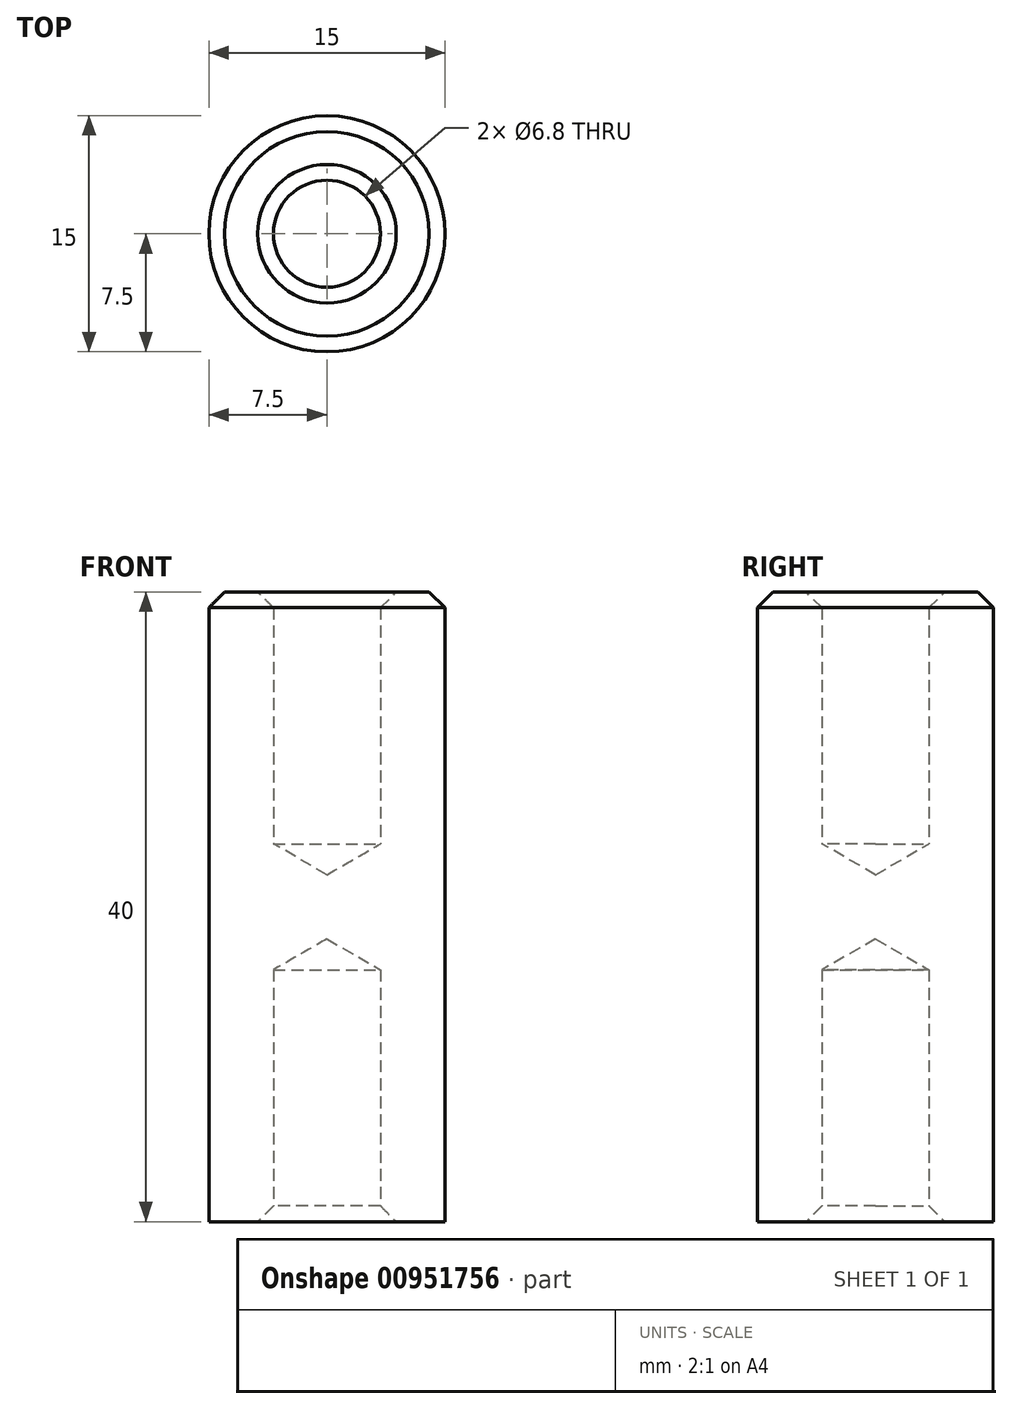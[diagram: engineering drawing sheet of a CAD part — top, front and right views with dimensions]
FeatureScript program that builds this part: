
annotation { "Feature Type Name" : "Feature", "Feature Type Description" : "" }
export const myFeature = defineFeature(function(context is Context, id is Id, definition is map)
    precondition{}
    {
        {
            var Q0;
            Q0=qCreatedBy(makeId("Front.planeOp"),FACE);
            var sketch = newSketch(context, id + "F0", { "sketchPlane" : qUnion([Q0])});
            skLineSegment(sketch, "E0", {"start": v(0, 0) * mm, "end": v(0, 66.91) * mm});
            skLineSegment(sketch, "E1", {"start": v(3.4, 0) * mm, "end": v(3.4, 16) * mm});
            skLineSegment(sketch, "E2", {"start": v(3.4, 16) * mm, "end": v(0, 17.96) * mm});
            skLineSegment(sketch, "E3", {"start": v(0, 17.96) * mm, "end": v(0, 22.04) * mm});
            skLineSegment(sketch, "E4", {"start": v(0, 22.04) * mm, "end": v(3.4, 24) * mm});
            skLineSegment(sketch, "E5", {"start": v(3.4, 24) * mm, "end": v(3.4, 40) * mm});
            skLineSegment(sketch, "E6", {"start": v(3.4, 40) * mm, "end": v(7.5, 40) * mm});
            skLineSegment(sketch, "E7", {"start": v(7.5, 40) * mm, "end": v(7.5, 0) * mm});
            skLineSegment(sketch, "E8", {"start": v(7.5, 0) * mm, "end": v(3.4, 0) * mm});
            skSolve(sketch);
        }
        {
            var Q0;
            Q0 = qSketchRegion(id + "F0", true);
            var Q1;
            Q1=sQuery(id+"F0.wireOp",EDGE,"E0");
            revolve(context, id + "F1", {"surfaceOperationType" : NewSurfaceOperationType.NEW, "entities" : qUnion([Q0]), "axis" : qUnion([Q1]), "revolveType" : RevolveType.FULL});
        }
        {
            var Q0;
            Q0=makeQuery(id+"F1.opRevolve","SWEPT_EDGE",EDGE,{"disambiguationData":[OSD([sQuery(id+"F0.wireOp",EDGE,"E6"),sQuery(id+"F0.wireOp",EDGE,"E7")])]});
            var Q1;
            Q1=makeQuery(id+"F1.opRevolve","SWEPT_EDGE",EDGE,{"disambiguationData":[OSD([sQuery(id+"F0.wireOp",EDGE,"E5"),sQuery(id+"F0.wireOp",EDGE,"E6")])]});
            var Q2;
            Q2=makeQuery(id+"F1.opRevolve","SWEPT_EDGE",EDGE,{"disambiguationData":[OSD([sQuery(id+"F0.wireOp",EDGE,"E1"),sQuery(id+"F0.wireOp",EDGE,"E8")])]});
            chamfer(context, id + "F2", {"entities" : qUnion([Q0, Q1, Q2]), "width" : 1 * mm, "tangentPropagation" : true});
        }
    });
